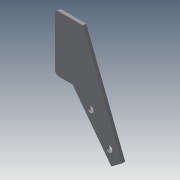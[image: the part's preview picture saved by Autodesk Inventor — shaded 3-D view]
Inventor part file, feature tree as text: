
AUTODESK INVENTOR PART (.ipt)
format: ipt  version: 2013 (Build 170138000, 138)  size: 210,944 bytes
history: native  units: mm
features: sketch x20, extrude x13, fillet x4
ambient origin geometry x8: Origin, YZ Plane, XZ Plane, XY Plane, X Axis, Y Axis, Z Axis, Center Point
bodies: Solid1 (feature_tree)
feature tree (37):
  sketch  "Sketch1"  dims[d4=3.0mm d5=3.0mm d6=2.0mm d7=0.0mm]
  extrude  "Extrusion1"  Depth=2.0mm TaperAngle=0.0deg
  extrude  "Extrusion2"  Depth=2.0mm TaperAngle=0.0deg
  extrude  "Extrusion3"  Depth=2.0mm TaperAngle=0.0deg
  sketch  "Sketch5"  dims[d19=0.5mm d20=0.0mm d21=10.0mm]
  extrude  "Extrusion4"  Depth=6.0mm TaperAngle=0.0deg
  sketch  "Sketch7"  dims[d25=1.5mm d26=0.0mm d27=10.0mm d28=0.0mm]
  sketch  "Sketch8"  dims[d29=2.0mm d30=2.0mm d31=10.0mm d32=0.0mm d33=6.5mm d34=0.0mm]
  extrude  "Extrusion5"  Depth=10.0mm
  sketch  "Sketch10"  dims[d39=2.0mm d43=0.01mm]
  extrude  "Extrusion6"  Depth=1.5mm TaperAngle=0.0deg
  extrude  "Extrusion7"  Depth=10.0mm TaperAngle=0.0deg
  extrude  "Extrusion8"  Depth=2.0mm
  fillet  "Fillet1"  Radius=10.0mm
  fillet  "Fillet2"  Radius=6.5mm
  sketch  "Sketch14"
  extrude  "Extrusion9"  Depth=2.0mm
  extrude  "Extrusion10"  Depth=0.01mm
  sketch  "Sketch17"
  sketch  "Sketch18"
  extrude  "Extrusion11"  Depth=0.2mm
  fillet  "Fillet3"  Radius=0.2mm
  fillet  "Fillet4"  Radius=10.0mm
  extrude  "Extrusion12"  [1 undecoded]
  extrude  "Extrusion13"  [1 undecoded]
  sketch  "Sketch2"  dims[d8=10.0mm d11=2.0mm d12=0.0mm]
  sketch  "Sketch3"  dims[d13=5.0mm d14=2.0mm d15=0.0mm]
  sketch  "Sketch4"  dims[d16=2.0mm d17=6.0mm d18=0.0mm]
  sketch  "Sketch6"  dims[d22=5.0mm d23=1.5mm d24=0.0mm]
  sketch  "Sketch9"  dims[d36=2.0mm d37=0.0mm d38=2.0mm]
  sketch  "Sketch11"  dims[d44=10.0mm d45=0.0mm d46=0.2mm d47=0.2mm d48=10.0mm d49=0.0mm]
  sketch  "Sketch12"
  sketch  "Sketch13"
  sketch  "Sketch15"
  sketch  "Sketch16"
  sketch  "Sketch19"
  sketch  "Sketch20"
note: 2 required parameter values undecoded (feature->parameter linkage not recoverable at this tier; creation-order binding heuristic only, values carry confidence <= 0.55)
